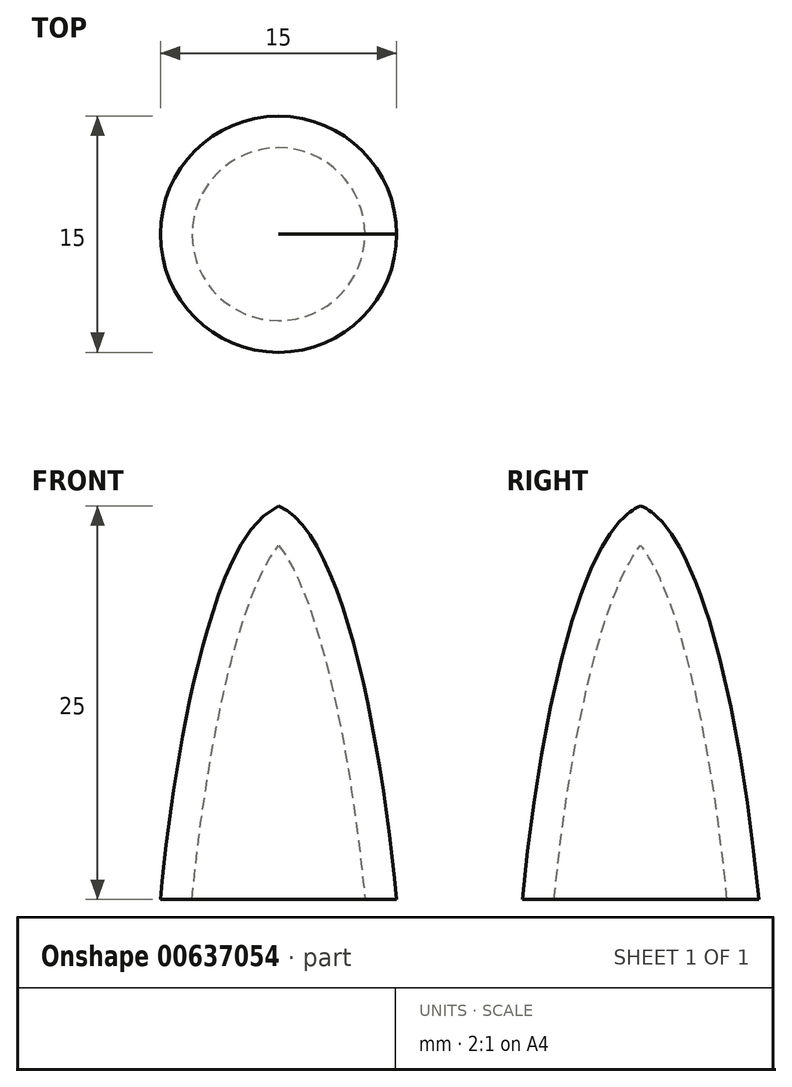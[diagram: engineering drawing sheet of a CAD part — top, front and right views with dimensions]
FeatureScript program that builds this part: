
annotation { "Feature Type Name" : "Feature", "Feature Type Description" : "" }
export const myFeature = defineFeature(function(context is Context, id is Id, definition is map)
    precondition{}
    {
        {
            var Q0;
            Q0=qCreatedBy(makeId("Front.planeOp"),FACE);
            var sketch = newSketch(context, id + "F0", { "sketchPlane" : qUnion([Q0])});
            skLineSegment(sketch, "E0", {"start": v(0, 0) * mm, "end": v(0, 25) * mm});
            skLineSegment(sketch, "E1", {"start": v(0, 0) * mm, "end": v(7.5, 0) * mm});
            skFitSpline(sketch, "E2", {"points": [v(0, 25) * mm, v(7.5, 0) * mm], "startDerivative": vector(12.29, -5.1) * mm, "endDerivative": vector(2.88, -30.4) * mm});
            skSolve(sketch);
        }
        {
            var Q0;
            Q0=makeQuery(id+"F0.imprint","IMPRINT",FACE,{"disambiguationData":[TD([[makeQuery(id+"F0.imprint","IMPRINT",EDGE,{"derivedFrom":sQuery(id+"F0.wireOp",EDGE,"E0")}),-1.0]])]});
            var Q1;
            Q1=sQuery(id+"F0.wireOp",EDGE,"E0");
            revolve(context, id + "F1", {"entities" : qUnion([Q0]), "axis" : qUnion([Q1]), "revolveType" : RevolveType.FULL});
        }
        {
            var Q0;
            Q0=makeQuery(id+"F1.opRevolve","SWEPT_FACE",FACE,{"disambiguationData":[OSD([sQuery(id+"F0.wireOp",EDGE,"E1")])]});
            shell(context, id + "F2", {"entities" : qUnion([Q0]), "thickness" : 2 * mm});
        }
    });
